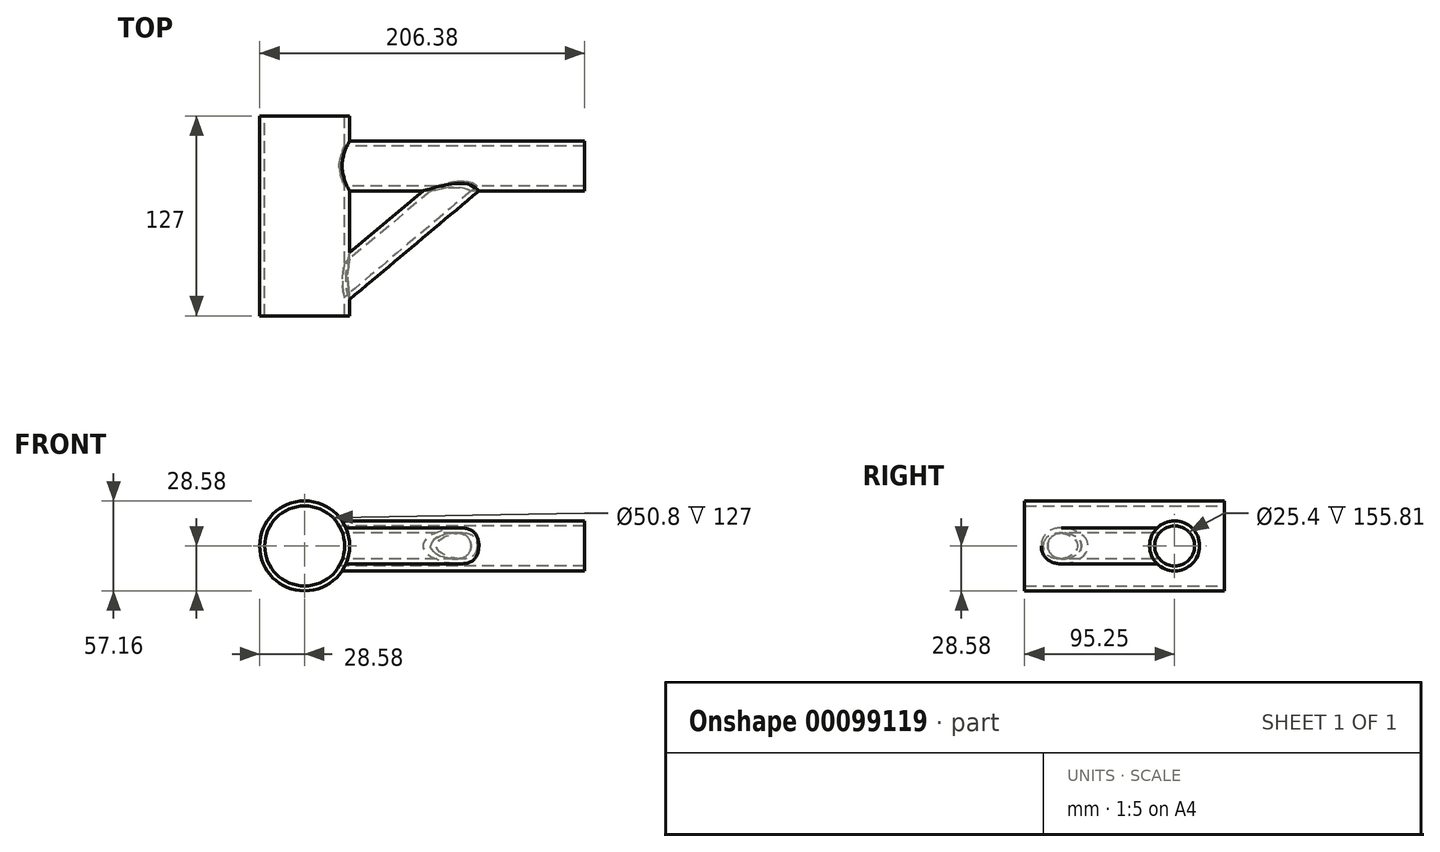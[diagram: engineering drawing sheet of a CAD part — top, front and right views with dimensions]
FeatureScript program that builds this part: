
annotation { "Feature Type Name" : "Feature", "Feature Type Description" : "" }
export const myFeature = defineFeature(function(context is Context, id is Id, definition is map)
    precondition{}
    {
        {
            var Q0;
            Q0=qCreatedBy(makeId("Front.planeOp"),FACE);
            var sketch = newSketch(context, id + "F0", { "sketchPlane" : qUnion([Q0])});
            skCircle(sketch, "E0", {"center": v(0, 0) * mm, "radius": 25.4 * mm});
            skCircle(sketch, "E1", {"center": v(0, 0) * mm, "radius": 28.58 * mm});
            skSolve(sketch);
        }
        {
            var Q0;
            Q0 = qSketchRegion(id + "F0", true);
            extrude(context, id + "F1", {"entities" : qUnion([Q0]), "depth" : 63.5 * mm, "hasSecondDirection" : true, "secondDirectionOppositeDirection" : true, "secondDirectionDepth" : 63.5 * mm});
        }
        {
            var Q0;
            Q0=qCreatedBy(makeId("Right.planeOp"),FACE);
            var sketch = newSketch(context, id + "F2", { "sketchPlane" : qUnion([Q0])});
            skCircle(sketch, "E2", {"center": v(31.75, 0) * mm, "radius": 12.7 * mm});
            skCircle(sketch, "E3", {"center": v(31.75, 0) * mm, "radius": 15.88 * mm});
            skSolve(sketch);
        }
        {
            var Q0;
            Q0 = qSketchRegion(id + "F2", true);
            extrude(context, id + "F3", {"entities" : qUnion([Q0]), "operationType" : NewBodyOperationType.ADD, "depth" : 177.8 * mm});
        }
        {
            var Q0;
            Q0=qCreatedBy(makeId("Front.planeOp"),FACE);
            var sketch = newSketch(context, id + "F4", { "sketchPlane" : qUnion([Q0])});
            skArc(sketch, "E4", {"start": v(19.65, -16.1) * mm, "mid": v(25.4, -0.14) * mm, "end": v(19.83, 15.88) * mm});
            skLineSegment(sketch, "E5", {"start": v(19.83, 15.88) * mm, "end": v(0, 15.88) * mm});
            skLineSegment(sketch, "E6", {"start": v(0, 15.88) * mm, "end": v(0, -16.02) * mm});
            skLineSegment(sketch, "E7", {"start": v(0, -16.02) * mm, "end": v(19.65, -16.1) * mm});
            skSolve(sketch);
        }
        {
            var Q0;
            Q0 = qSketchRegion(id + "F4", true);
            extrude(context, id + "F5", {"entities" : qUnion([Q0]), "operationType" : NewBodyOperationType.REMOVE, "oppositeDirection" : true, "depth" : 76.2 * mm});
        }
        {
            var Q0;
            Q0=qCreatedBy(makeId("Right.planeOp"),FACE);
            var sketch = newSketch(context, id + "F6", { "sketchPlane" : qUnion([Q0])});
            skCircle(sketch, "E8", {"center": v(31.75, 0) * mm, "radius": 12.7 * mm});
            skSolve(sketch);
        }
        {
            var Q0;
            Q0 = qSketchRegion(id + "F6", true);
            extrude(context, id + "F7", {"entities" : qUnion([Q0]), "operationType" : NewBodyOperationType.REMOVE, "depth" : 31.75 * mm});
        }
        {
            var Q0;
            Q0=qCreatedBy(makeId("Front.planeOp"),FACE);
            var sketch = newSketch(context, id + "F8", { "sketchPlane" : qUnion([Q0])});
            skLineSegment(sketch, "E9", {"start": v(92.26, 55.32) * mm, "end": v(92.26, -49.18) * mm});
            skSolve(sketch);
        }
        {
            var Q0;
            Q0=qCreatedBy(makeId("Front.planeOp"),FACE);
            var sketch = newSketch(context, id + "F9", { "sketchPlane" : qUnion([Q0])});
            skCircle(sketch, "E10", {"center": v(80.48, 0.02) * mm, "radius": 8.26 * mm});
            skCircle(sketch, "E11", {"center": v(80.48, 0.02) * mm, "radius": 11.43 * mm});
            skLineSegment(sketch, "E12", {"start": v(80.48, 26.17) * mm, "end": v(80.48, -31.54) * mm});
            skSolve(sketch);
        }
        {
            var Q0;
            {var subQ0=sQuery(id+"F9.wireOp",EDGE,"N99zYOHZ-lHou-g50B-YFcY-hyawqMIxnTmh");var subQ1=sQuery(id+"F9.wireOp",EDGE,"E10");var subQ2=makeQuery(id+"F9.imprint","INTERSECT",VERTEX,{"derivedFrom":[subQ1,subQ0]});Q0=makeQuery(id+"F9.imprint","IMPRINT",FACE,{"disambiguationData":[TD([[makeQuery(id+"F9.imprint","IMPRINT",EDGE,{"disambiguationData":[TD([[subQ2,1.0]])],"derivedFrom":subQ1}),1.0]])]});}
            var Q1;
            {var subQ0=sQuery(id+"F9.wireOp",EDGE,"N99zYOHZ-lHou-g50B-YFcY-hyawqMIxnTmh");var subQ1=sQuery(id+"F9.wireOp",EDGE,"E10");var subQ2=makeQuery(id+"F9.imprint","INTERSECT",VERTEX,{"derivedFrom":[subQ1,subQ0]});Q1=makeQuery(id+"F9.imprint","IMPRINT",FACE,{"disambiguationData":[TD([[makeQuery(id+"F9.imprint","IMPRINT",EDGE,{"disambiguationData":[TD([[subQ2,-1.0]])],"derivedFrom":subQ1}),1.0]])]});}
            var Q2;
            {var subQ0=sQuery(id+"F2.wireOp",EDGE,"E3");Q2=makeQuery(id+"F3.boolean.opBoolean","SPLIT",FACE,{"disambiguationData":[TD([makeQuery(id+"F1.opExtrude","SWEPT_FACE",FACE,{"disambiguationData":[OSD([sQuery(id+"F0.wireOp",EDGE,"E1")])]})])],"derivedFrom":makeQuery(id+"F3.opExtrude","SWEPT_FACE",FACE,{"disambiguationData":[OSD([subQ0])]})});}
            var Q3;
            Q3=makeQuery(id+"F1.opExtrude","SWEPT_BODY",BODY,{"disambiguationData":[OSD([sQuery(id+"F0.wireOp",EDGE,"E0"),sQuery(id+"F0.wireOp",EDGE,"E1")])]});
            extrude(context, id + "F10", {"entities" : qUnion([Q0, Q1]), "depth" : 101.6 * mm, "hasSecondDirection" : true, "secondDirectionBound" : SecondDirectionBoundingType.UP_TO_SURFACE, "secondDirectionOppositeDirection" : true, "secondDirectionBoundEntityFace" : qUnion([Q2]), "secondDirectionBoundEntityBody" : qUnion([Q3]), "secondDirectionDepth" : 25.4 * mm});
        }
        {
            var Q0;
            Q0=makeQuery(id+"F10.opExtrude","SWEPT_BODY",BODY,{"disambiguationData":[OSD([sQuery(id+"F9.wireOp",EDGE,"E10")])]});
            var Q1;
            Q1=sQuery(id+"F8.wireOp",EDGE,"E9");
            transform(context, id + "F11", {"entities" : qUnion([Q0]), "transformType" : TransformType.ROTATION, "transformAxis" : qUnion([Q1]), "angle" : 50 * degree, "makeCopy" : false});
        }
        {
            var Q0;
            Q0=makeQuery(id+"F10.opExtrude","CAP_FACE",FACE,{"disambiguationData":[OSD([sQuery(id+"F9.wireOp",EDGE,"E10")])],"isStart":false});
            var sketch = newSketch(context, id + "F12", { "sketchPlane" : qUnion([Q0])});
            skCircle(sketch, "E13", {"center": v(47.53, 0.02) * mm, "radius": 11.43 * mm});
            skSolve(sketch);
        }
        {
            var Q0;
            Q0=makeQuery(id+"F12.imprint","IMPRINT",FACE,{"disambiguationData":[TD([[makeQuery(id+"F12.imprint","IMPRINT",EDGE,{"derivedFrom":sQuery(id+"F12.wireOp",EDGE,"E13")}),1.0]])]});
            var Q1;
            {var subQ0=sQuery(id+"F2.wireOp",EDGE,"E3");Q1=makeQuery(id+"F3.boolean.opBoolean","SPLIT",FACE,{"disambiguationData":[TD([makeQuery(id+"F1.opExtrude","SWEPT_FACE",FACE,{"disambiguationData":[OSD([sQuery(id+"F0.wireOp",EDGE,"E1")])]})])],"derivedFrom":makeQuery(id+"F3.opExtrude","SWEPT_FACE",FACE,{"disambiguationData":[OSD([subQ0])]})});}
            var Q2;
            {var subQ0=sQuery(id+"F0.wireOp",EDGE,"E1");Q2=makeQuery(id+"F3.boolean.opBoolean","SPLIT",FACE,{"disambiguationData":[TD([makeQuery(id+"F3.opExtrude","SWEPT_FACE",FACE,{"disambiguationData":[OSD([sQuery(id+"F2.wireOp",EDGE,"E3")])]})])],"derivedFrom":makeQuery(id+"F1.opExtrude","SWEPT_FACE",FACE,{"disambiguationData":[OSD([subQ0])]})});}
            extrude(context, id + "F13", {"entities" : qUnion([Q0]), "endBound" : BoundingType.UP_TO_SURFACE, "oppositeDirection" : true, "endBoundEntityFace" : qUnion([Q1]), "depth" : 130.8 * mm, "hasSecondDirection" : true, "secondDirectionBound" : SecondDirectionBoundingType.UP_TO_SURFACE, "secondDirectionOppositeDirection" : true, "secondDirectionBoundEntityFace" : qUnion([Q2]), "secondDirectionDepth" : 12.7 * mm});
        }
        {
            var Q0;
            Q0=makeQuery(id+"F10.opExtrude","CAP_FACE",FACE,{"disambiguationData":[OSD([sQuery(id+"F9.wireOp",EDGE,"E10")])],"isStart":false});
            var sketch = newSketch(context, id + "F14", { "sketchPlane" : qUnion([Q0])});
            skCircle(sketch, "E14", {"center": v(47.53, 0.02) * mm, "radius": 8.26 * mm});
            skSolve(sketch);
        }
        {
            var Q0;
            Q0 = qSketchRegion(id + "F14", true);
            extrude(context, id + "F15", {"entities" : qUnion([Q0]), "operationType" : NewBodyOperationType.REMOVE, "oppositeDirection" : true, "depth" : 134.62 * mm});
        }
    });
